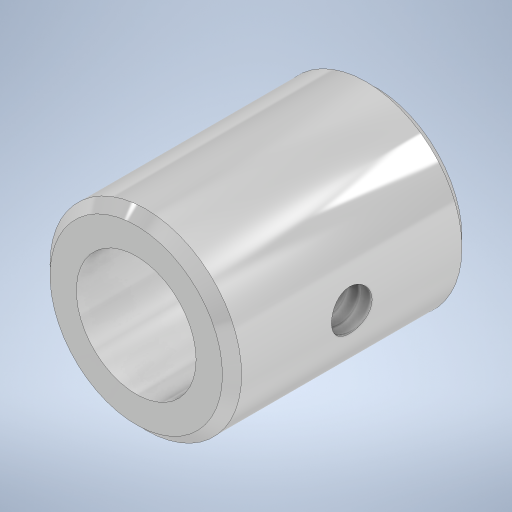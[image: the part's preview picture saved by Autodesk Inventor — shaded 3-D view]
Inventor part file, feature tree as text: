
AUTODESK INVENTOR PART (.ipt)
format: ipt  version: 2023 (Build 270158000, 158)  size: 260,096 bytes
history: native  units: in
note: dims shown in document units (in); Inventor stores cm internally (conversion verified against a paired STEP export)
features: sketch x2, extrude x1, chamfer x1, plane x1, hole x1
ambient origin geometry x8: Origin, YZ Plane, XZ Plane, XY Plane, X Axis, Y Axis, Z Axis, Center Point
bodies: Solid1 (feature_tree)
feature tree (6):
  extrude  "Extrusion1"  Depth=0.4in
  chamfer  "Chamfer1"  Distance=0.5in
  plane  "Work Plane1"
  hole  "Hole1"  [1 undecoded]
  sketch  "Sketch1"  dims[d0=0.25in d1=0.4in d2=0.5in d3=0.0in]
  sketch  "Sketch2"  dims[d4=0.02in d5=0.125in d6=45.0deg d7=0.25in d8=0.25in d9=0.0849in d10=0.224in d11=0.173in d12=0.079in d13=90.0deg d14=0.25in d15=0.0in]
note: 1 required parameter value undecoded (feature->parameter linkage not recoverable at this tier; creation-order binding heuristic only, values carry confidence <= 0.55)
